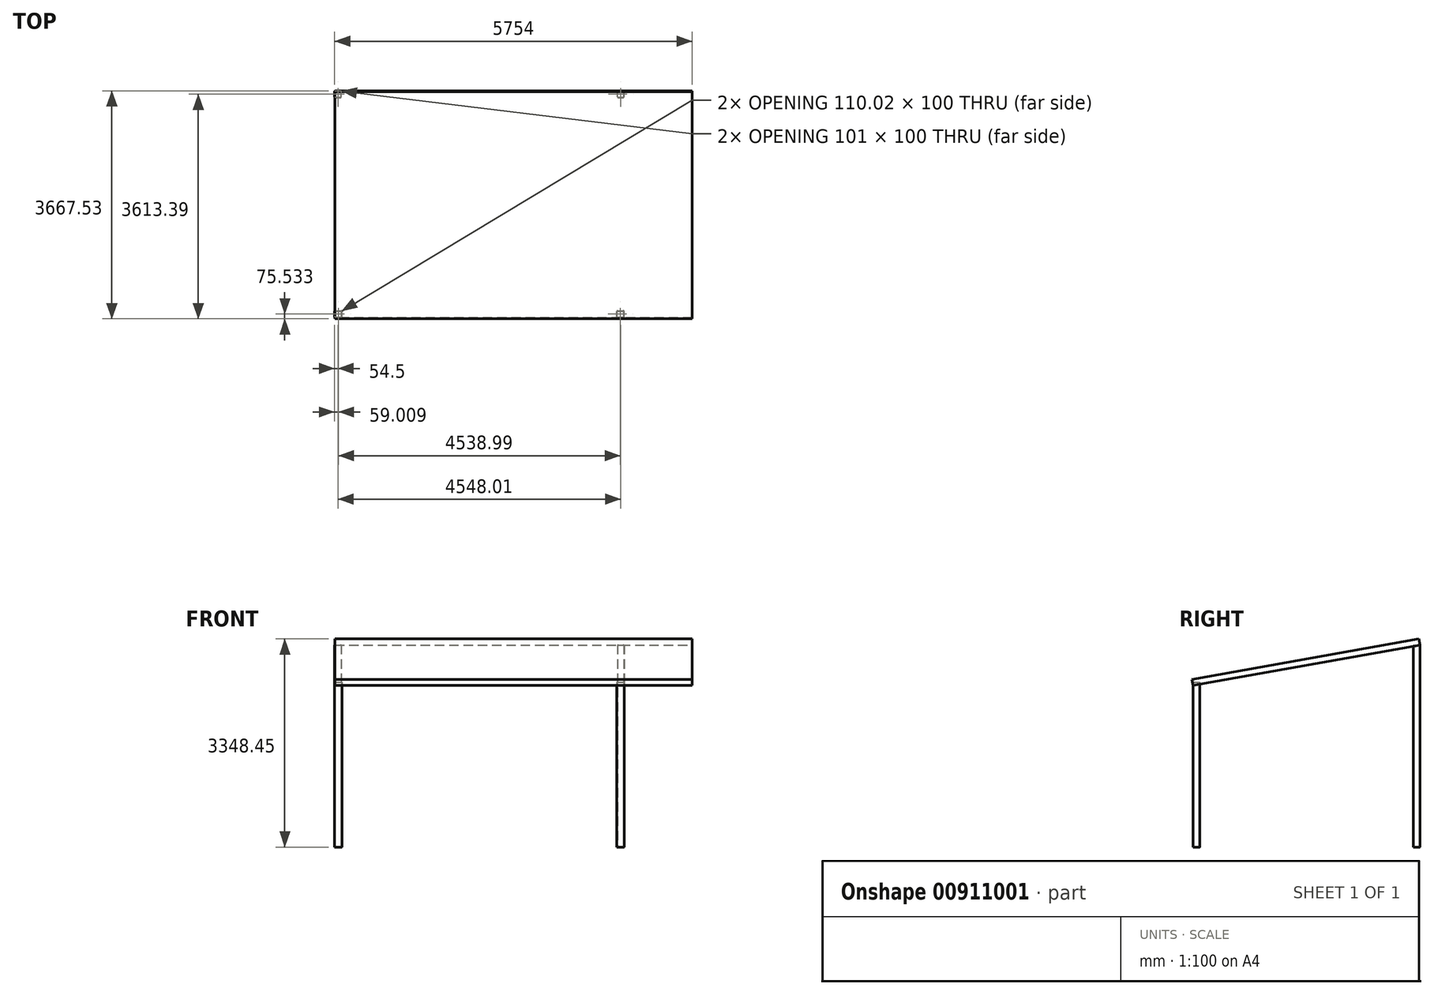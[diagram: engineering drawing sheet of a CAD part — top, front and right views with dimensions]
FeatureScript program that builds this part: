
annotation { "Feature Type Name" : "Feature", "Feature Type Description" : "" }
export const myFeature = defineFeature(function(context is Context, id is Id, definition is map)
    precondition{}
    {
        {
            var Q0;
            Q0=qCreatedBy(makeId("Front.planeOp"),FACE);
            var sketch = newSketch(context, id + "F0", { "sketchPlane" : qUnion([Q0])});
            skLineSegment(sketch, "E0", {"start": v(0, 0) * mm, "end": v(0, 2600) * mm});
            skLineSegment(sketch, "E1", {"start": v(4600, 0) * mm, "end": v(4600, 2600) * mm});
            skSolve(sketch);
        }
        {
            var Q0;
            Q0=qCreatedBy(makeId("Front.planeOp"),FACE);
            cPlane(context, id + "F1", {"entities" : qUnion([Q0]), "cplaneType" : CPlaneType.OFFSET, "offset" : 3650 * mm, "oppositeDirection" : true, "width" : 150 * mm, "height" : 150 * mm});
        }
        {
            var Q0;
            Q0=qCreatedBy(id+"F1.planeOp",FACE);
            var sketch = newSketch(context, id + "F2", { "sketchPlane" : qUnion([Q0])});
            skLineSegment(sketch, "E2", {"start": v(0, 0) * mm, "end": v(0, 3250) * mm});
            skLineSegment(sketch, "E3", {"start": v(4600, 0) * mm, "end": v(4600, 3250) * mm});
            skSolve(sketch);
        }
        {
            var Q0;
            Q0=qCreatedBy(makeId("Top.planeOp"),FACE);
            var sketch = newSketch(context, id + "F3", { "sketchPlane" : qUnion([Q0])});
            skLineSegment(sketch, "E4.bottom", {"start": v(10, 8) * mm, "end": v(100.02, 8) * mm});
            skLineSegment(sketch, "E4.top", {"start": v(10, 108) * mm, "end": v(100.02, 108) * mm});
            skLineSegment(sketch, "E4.left", {"start": v(0, 18) * mm, "end": v(0, 98) * mm});
            skLineSegment(sketch, "E4.right", {"start": v(110.02, 18) * mm, "end": v(110.02, 98) * mm});
            skPoint(sketch, "E5.visualSharp", {"position": v(0, 108) * mm});
            skArc(sketch, "E5.filletArc", {"start": v(10, 108) * mm, "mid": v(2.93, 105.07) * mm, "end": v(0, 98) * mm});
            skPoint(sketch, "E6.visualSharp", {"position": v(110.02, 108) * mm});
            skArc(sketch, "E6.filletArc", {"start": v(110.02, 98) * mm, "mid": v(107.09, 105.07) * mm, "end": v(100.02, 108) * mm});
            skPoint(sketch, "E7.visualSharp", {"position": v(110.02, 8) * mm});
            skArc(sketch, "E7.filletArc", {"start": v(100.02, 8) * mm, "mid": v(107.09, 10.93) * mm, "end": v(110.02, 18) * mm});
            skPoint(sketch, "E8.visualSharp", {"position": v(9.02, 8) * mm});
            skArc(sketch, "E8.filletArc", {"start": v(0, 18) * mm, "mid": v(2.93, 10.93) * mm, "end": v(10, 8) * mm});
            skPoint(sketch, "E9.visualSharp", {"position": v(13.02, 104) * mm});
            skArc(sketch, "E10.0", {"start": v(100.02, 4) * mm, "mid": v(109.92, 8.1) * mm, "end": v(114.02, 18) * mm});
            skLineSegment(sketch, "E10.1", {"start": v(10, 4) * mm, "end": v(100.02, 4) * mm});
            skLineSegment(sketch, "E10.2", {"start": v(114.02, 18) * mm, "end": v(114.02, 98) * mm});
            skArc(sketch, "E10.3", {"start": v(-4, 18) * mm, "mid": v(0.1, 8.1) * mm, "end": v(10, 4) * mm});
            skArc(sketch, "E10.4", {"start": v(114.02, 98) * mm, "mid": v(109.92, 107.9) * mm, "end": v(100.02, 112) * mm});
            skLineSegment(sketch, "E10.5", {"start": v(10, 112) * mm, "end": v(100.02, 112) * mm});
            skArc(sketch, "E10.6", {"start": v(10, 112) * mm, "mid": v(0.1, 107.9) * mm, "end": v(-4, 98) * mm});
            skLineSegment(sketch, "E10.7", {"start": v(-4, 18) * mm, "end": v(-4, 98) * mm});
            skLineSegment(sketch, "E11.bottom", {"start": v(10, 3545.86) * mm, "end": v(91, 3545.86) * mm});
            skLineSegment(sketch, "E11.top", {"start": v(10, 3645.86) * mm, "end": v(91, 3645.86) * mm});
            skLineSegment(sketch, "E11.left", {"start": v(0, 3555.86) * mm, "end": v(0, 3635.86) * mm});
            skLineSegment(sketch, "E11.right", {"start": v(101, 3555.86) * mm, "end": v(101, 3635.86) * mm});
            skPoint(sketch, "E12.visualSharp", {"position": v(0, 3645.86) * mm});
            skArc(sketch, "E12.filletArc", {"start": v(10, 3645.86) * mm, "mid": v(2.93, 3642.93) * mm, "end": v(0, 3635.86) * mm});
            skPoint(sketch, "E13.visualSharp", {"position": v(101, 3645.86) * mm});
            skArc(sketch, "E13.filletArc", {"start": v(101, 3635.86) * mm, "mid": v(98.07, 3642.93) * mm, "end": v(91, 3645.86) * mm});
            skPoint(sketch, "E14.visualSharp", {"position": v(101, 3545.86) * mm});
            skArc(sketch, "E14.filletArc", {"start": v(91, 3545.86) * mm, "mid": v(98.07, 3548.79) * mm, "end": v(101, 3555.86) * mm});
            skPoint(sketch, "E15.visualSharp", {"position": v(0, 3545.86) * mm});
            skArc(sketch, "E15.filletArc", {"start": v(0, 3555.86) * mm, "mid": v(2.93, 3548.79) * mm, "end": v(10, 3545.86) * mm});
            skPoint(sketch, "E16.visualSharp", {"position": v(4, 3641.86) * mm});
            skArc(sketch, "E17.0", {"start": v(91, 3541.86) * mm, "mid": v(100.9, 3545.96) * mm, "end": v(105, 3555.86) * mm});
            skLineSegment(sketch, "E17.1", {"start": v(10, 3541.86) * mm, "end": v(91, 3541.86) * mm});
            skLineSegment(sketch, "E17.2", {"start": v(105, 3555.86) * mm, "end": v(105, 3635.86) * mm});
            skArc(sketch, "E17.3", {"start": v(-4, 3555.86) * mm, "mid": v(0.1, 3545.96) * mm, "end": v(10, 3541.86) * mm});
            skArc(sketch, "E17.4", {"start": v(105, 3635.86) * mm, "mid": v(100.9, 3645.76) * mm, "end": v(91, 3649.86) * mm});
            skLineSegment(sketch, "E17.5", {"start": v(10, 3649.86) * mm, "end": v(91, 3649.86) * mm});
            skArc(sketch, "E17.6", {"start": v(10, 3649.86) * mm, "mid": v(0.1, 3645.76) * mm, "end": v(-4, 3635.86) * mm});
            skLineSegment(sketch, "E17.7", {"start": v(-4, 3555.86) * mm, "end": v(-4, 3635.86) * mm});
            skLineSegment(sketch, "E18.bottom", {"start": v(4558.01, 3545.86) * mm, "end": v(4639.01, 3545.86) * mm});
            skLineSegment(sketch, "E18.top", {"start": v(4558.01, 3645.86) * mm, "end": v(4639.01, 3645.86) * mm});
            skLineSegment(sketch, "E18.left", {"start": v(4548.01, 3555.86) * mm, "end": v(4548.01, 3635.86) * mm});
            skLineSegment(sketch, "E18.right", {"start": v(4649.01, 3555.86) * mm, "end": v(4649.01, 3635.86) * mm});
            skPoint(sketch, "E19.visualSharp", {"position": v(4548.01, 3645.86) * mm});
            skArc(sketch, "E19.filletArc", {"start": v(4558.01, 3645.86) * mm, "mid": v(4550.94, 3642.93) * mm, "end": v(4548.01, 3635.86) * mm});
            skPoint(sketch, "E20.visualSharp", {"position": v(4649.01, 3645.86) * mm});
            skArc(sketch, "E20.filletArc", {"start": v(4649.01, 3635.86) * mm, "mid": v(4646.08, 3642.93) * mm, "end": v(4639.01, 3645.86) * mm});
            skPoint(sketch, "E21.visualSharp", {"position": v(4649.01, 3545.86) * mm});
            skArc(sketch, "E21.filletArc", {"start": v(4639.01, 3545.86) * mm, "mid": v(4646.08, 3548.79) * mm, "end": v(4649.01, 3555.86) * mm});
            skPoint(sketch, "E22.visualSharp", {"position": v(4548.01, 3545.86) * mm});
            skArc(sketch, "E22.filletArc", {"start": v(4548.01, 3555.86) * mm, "mid": v(4550.94, 3548.79) * mm, "end": v(4558.01, 3545.86) * mm});
            skPoint(sketch, "E23.visualSharp", {"position": v(4552.01, 3641.86) * mm});
            skArc(sketch, "E24.0", {"start": v(4639.01, 3541.86) * mm, "mid": v(4648.91, 3545.96) * mm, "end": v(4653.01, 3555.86) * mm});
            skLineSegment(sketch, "E24.1", {"start": v(4558.01, 3541.86) * mm, "end": v(4639.01, 3541.86) * mm});
            skLineSegment(sketch, "E24.2", {"start": v(4653.01, 3555.86) * mm, "end": v(4653.01, 3635.86) * mm});
            skArc(sketch, "E24.3", {"start": v(4544.01, 3555.86) * mm, "mid": v(4548.11, 3545.96) * mm, "end": v(4558.01, 3541.86) * mm});
            skArc(sketch, "E24.4", {"start": v(4653.01, 3635.86) * mm, "mid": v(4648.91, 3645.76) * mm, "end": v(4639.01, 3649.86) * mm});
            skLineSegment(sketch, "E24.5", {"start": v(4558.01, 3649.86) * mm, "end": v(4639.01, 3649.86) * mm});
            skArc(sketch, "E24.6", {"start": v(4558.01, 3649.86) * mm, "mid": v(4548.11, 3645.76) * mm, "end": v(4544.01, 3635.86) * mm});
            skLineSegment(sketch, "E24.7", {"start": v(4544.01, 3555.86) * mm, "end": v(4544.01, 3635.86) * mm});
            skLineSegment(sketch, "E25.bottom", {"start": v(4549, 8) * mm, "end": v(4639.01, 8) * mm});
            skLineSegment(sketch, "E25.top", {"start": v(4549, 108) * mm, "end": v(4639.01, 108) * mm});
            skLineSegment(sketch, "E25.left", {"start": v(4539, 18) * mm, "end": v(4539, 98) * mm});
            skLineSegment(sketch, "E25.right", {"start": v(4649.01, 18) * mm, "end": v(4649.01, 98) * mm});
            skPoint(sketch, "E26.visualSharp", {"position": v(4539, 108) * mm});
            skArc(sketch, "E26.filletArc", {"start": v(4549, 108) * mm, "mid": v(4541.92, 105.07) * mm, "end": v(4539, 98) * mm});
            skPoint(sketch, "E27.visualSharp", {"position": v(4649.01, 108) * mm});
            skArc(sketch, "E27.filletArc", {"start": v(4649.01, 98) * mm, "mid": v(4646.08, 105.07) * mm, "end": v(4639.01, 108) * mm});
            skPoint(sketch, "E28.visualSharp", {"position": v(4649.01, 8) * mm});
            skArc(sketch, "E28.filletArc", {"start": v(4639.01, 8) * mm, "mid": v(4646.08, 10.93) * mm, "end": v(4649.01, 18) * mm});
            skPoint(sketch, "E29.visualSharp", {"position": v(4548.01, 4) * mm});
            skArc(sketch, "E29.filletArc", {"start": v(4539, 18) * mm, "mid": v(4541.92, 10.93) * mm, "end": v(4549, 8) * mm});
            skPoint(sketch, "E30.visualSharp", {"position": v(4552.01, 100) * mm});
            skArc(sketch, "E31.0", {"start": v(4639.01, 4) * mm, "mid": v(4648.91, 8.1) * mm, "end": v(4653.01, 18) * mm});
            skLineSegment(sketch, "E31.1", {"start": v(4549, 4) * mm, "end": v(4639.01, 4) * mm});
            skLineSegment(sketch, "E31.2", {"start": v(4653.01, 18) * mm, "end": v(4653.01, 98) * mm});
            skArc(sketch, "E31.3", {"start": v(4535, 18) * mm, "mid": v(4539.1, 8.1) * mm, "end": v(4549, 4) * mm});
            skArc(sketch, "E31.4", {"start": v(4653.01, 98) * mm, "mid": v(4648.91, 107.9) * mm, "end": v(4639.01, 112) * mm});
            skLineSegment(sketch, "E31.5", {"start": v(4549, 112) * mm, "end": v(4639.01, 112) * mm});
            skArc(sketch, "E31.6", {"start": v(4549, 112) * mm, "mid": v(4539.1, 107.9) * mm, "end": v(4535, 98) * mm});
            skLineSegment(sketch, "E31.7", {"start": v(4535, 18) * mm, "end": v(4535, 98) * mm});
            skSolve(sketch);
        }
        {
            var Q0;
            Q0=qCreatedBy(makeId("Right.planeOp"),FACE);
            var sketch = newSketch(context, id + "F4", { "sketchPlane" : qUnion([Q0])});
            skLineSegment(sketch, "E32", {"start": v(3650, 3250) * mm, "end": v(0, 2600) * mm});
            skSolve(sketch);
        }
        {
            var Q0;
            Q0=qCreatedBy(makeId("Right.planeOp"),FACE);
            cPlane(context, id + "F5", {"entities" : qUnion([Q0]), "cplaneType" : CPlaneType.OFFSET, "offset" : 4600 * mm, "width" : 150 * mm, "height" : 150 * mm});
        }
        {
            var Q0;
            Q0=qCreatedBy(id+"F1.planeOp",FACE);
            var sketch = newSketch(context, id + "F6", { "sketchPlane" : qUnion([Q0])});
            skLineSegment(sketch, "E33.0", {"start": v(0, 0) * mm, "end": v(0, 3250) * mm});
            skLineSegment(sketch, "E34.0", {"start": v(4600, 0) * mm, "end": v(4600, 3250) * mm});
            skLineSegment(sketch, "E35.0", {"start": v(0, 0) * mm, "end": v(0, 2600) * mm});
            skPoint(sketch, "E36.0", {"position": v(4600, 1300) * mm});
            skLineSegment(sketch, "E37", {"start": v(0, 3250) * mm, "end": v(4600, 3250) * mm});
            skLineSegment(sketch, "E38", {"start": v(4600, 3250) * mm, "end": v(5750, 3250) * mm});
            skSolve(sketch);
        }
        {
            var Q0;
            Q0=qCreatedBy(makeId("Front.planeOp"),FACE);
            var sketch = newSketch(context, id + "F7", { "sketchPlane" : qUnion([Q0])});
            skLineSegment(sketch, "E39.0", {"start": v(0, 0) * mm, "end": v(0, 2600) * mm});
            skLineSegment(sketch, "E40.0", {"start": v(4600, 0) * mm, "end": v(4600, 2600) * mm});
            skLineSegment(sketch, "E41", {"start": v(0, 2600) * mm, "end": v(4600, 2600) * mm});
            skLineSegment(sketch, "E42", {"start": v(4600, 2600) * mm, "end": v(5750, 2600) * mm});
            skSolve(sketch);
        }
        {
            var Q0;
            Q0=qCreatedBy(id+"F5.planeOp",FACE);
            cPlane(context, id + "F8", {"entities" : qUnion([Q0]), "cplaneType" : CPlaneType.OFFSET, "offset" : 1150 * mm, "width" : 150 * mm, "height" : 150 * mm});
        }
        {
            var Q0;
            Q0=qCreatedBy(id+"F8.planeOp",FACE);
            var sketch = newSketch(context, id + "F9", { "sketchPlane" : qUnion([Q0])});
            skLineSegment(sketch, "E43", {"start": v(3650, 3250) * mm, "end": v(0, 2600) * mm});
            skSolve(sketch);
        }
        {
            var Q0;
            Q0=sQuery(id+"F6.wireOp",EDGE,"E37");
            var Q1;
            Q1=sQuery(id+"F7.wireOp",EDGE,"E41");
            cPlane(context, id + "F10", {"entities" : qUnion([Q0, Q1]), "cplaneType" : CPlaneType.LINE_ANGLE, "offset" : 25 * mm, "angle" : 0 * degree, "width" : 150 * mm, "height" : 150 * mm});
        }
        {
            var Q0;
            Q0=qCreatedBy(id+"F10.planeOp",FACE);
            var sketch = newSketch(context, id + "F11", { "sketchPlane" : qUnion([Q0])});
            skLineSegment(sketch, "E44.0", {"start": v(0, -4163.27) * mm, "end": v(0, -455.84) * mm});
            skLineSegment(sketch, "E45.0", {"start": v(5750, -4163.27) * mm, "end": v(5750, -455.84) * mm});
            skLineSegment(sketch, "E46", {"start": v(0, -4163.27) * mm, "end": v(5750, -4163.27) * mm});
            skLineSegment(sketch, "E47", {"start": v(5750, -455.84) * mm, "end": v(0, -455.84) * mm});
            skSolve(sketch);
        }
        {
            var Q0;
            Q0=makeQuery(id+"F11.imprint","IMPRINT",FACE,{"disambiguationData":[TD([[makeQuery(id+"F11.imprint","IMPRINT",EDGE,{"derivedFrom":sQuery(id+"F11.wireOp",EDGE,"E44.0")}),-1.0]])]});
            extrude(context, id + "F12", {"entities" : qUnion([Q0]), "oppositeDirection" : true, "depth" : 100 * mm, "offsetDistance" : 25 * mm});
        }
        {
            var Q0;
            Q0=makeQuery(id+"F3.imprint","IMPRINT",FACE,{"disambiguationData":[TD([[makeQuery(id+"F3.imprint","IMPRINT",EDGE,{"derivedFrom":sQuery(id+"F3.wireOp",EDGE,"E4.bottom")}),-1.0]])]});
            var Q1;
            Q1=makeQuery(id+"F3.imprint","IMPRINT",FACE,{"disambiguationData":[TD([[makeQuery(id+"F3.imprint","IMPRINT",EDGE,{"derivedFrom":sQuery(id+"F3.wireOp",EDGE,"E25.bottom")}),-1.0]])]});
            extrude(context, id + "F13", {"entities" : qUnion([Q0, Q1]), "depth" : 2650 * mm, "offsetDistance" : 25 * mm});
        }
        {
            var Q0;
            Q0=makeQuery(id+"F3.imprint","IMPRINT",FACE,{"disambiguationData":[TD([[makeQuery(id+"F3.imprint","IMPRINT",EDGE,{"derivedFrom":sQuery(id+"F3.wireOp",EDGE,"E11.bottom")}),-1.0]])]});
            var Q1;
            Q1=makeQuery(id+"F3.imprint","IMPRINT",FACE,{"disambiguationData":[TD([[makeQuery(id+"F3.imprint","IMPRINT",EDGE,{"derivedFrom":sQuery(id+"F3.wireOp",EDGE,"E18.bottom")}),-1.0]])]});
            extrude(context, id + "F14", {"entities" : qUnion([Q0, Q1]), "depth" : 3250 * mm, "offsetDistance" : 25 * mm});
        }
    });
